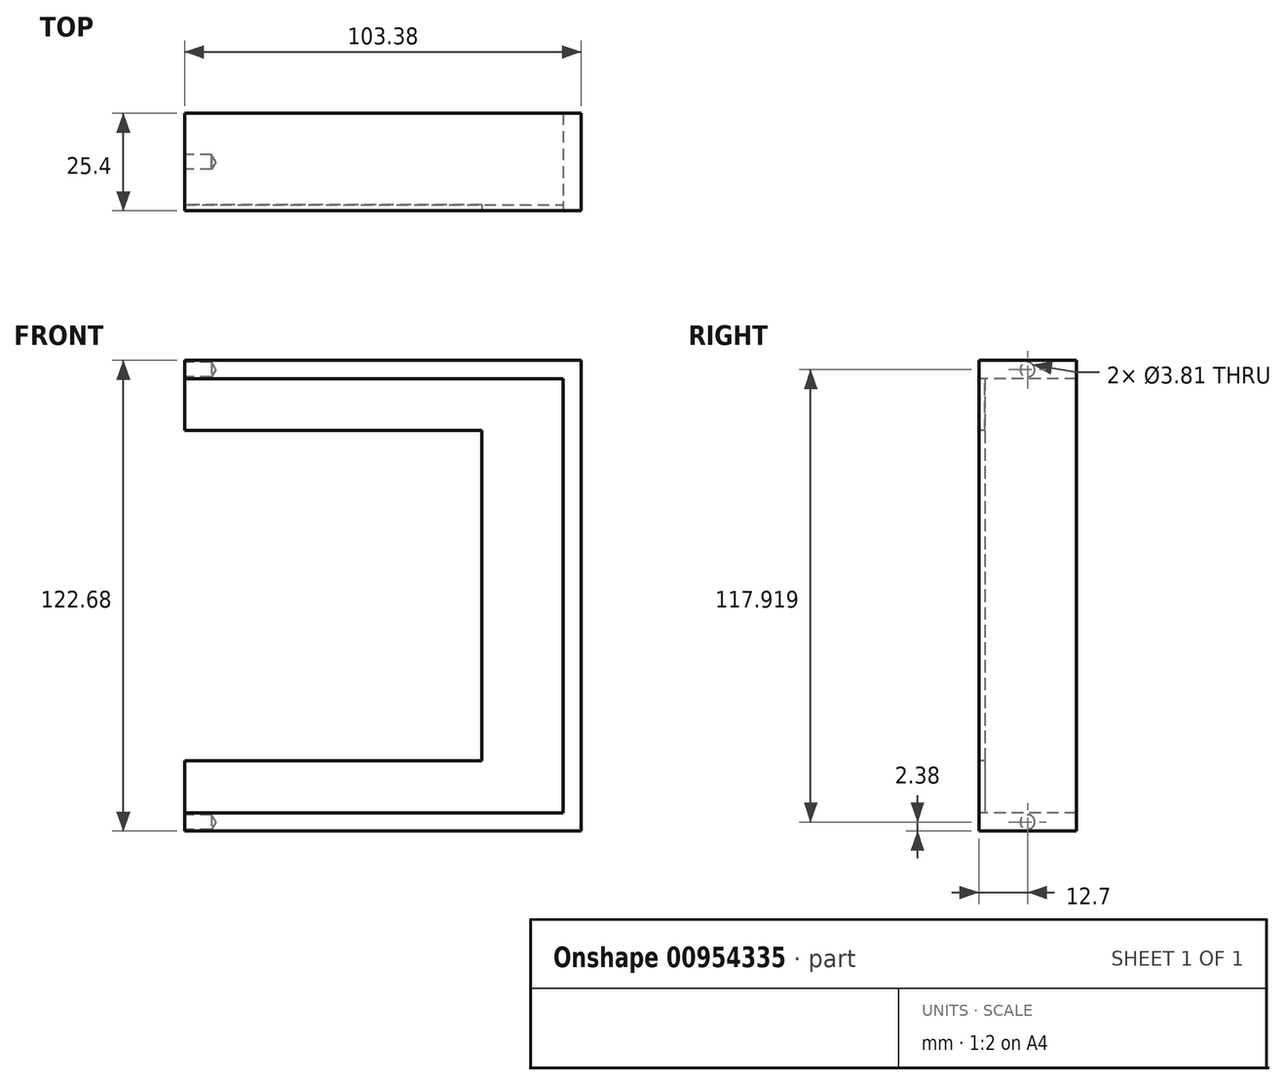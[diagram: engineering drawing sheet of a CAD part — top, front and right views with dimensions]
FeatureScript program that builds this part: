
annotation { "Feature Type Name" : "Feature", "Feature Type Description" : "" }
export const myFeature = defineFeature(function(context is Context, id is Id, definition is map)
    precondition{}
    {
        {
            var Q0;
            Q0=qCreatedBy(makeId("Front.planeOp"),FACE);
            var sketch = newSketch(context, id + "F0", { "sketchPlane" : qUnion([Q0])});
            skLineSegment(sketch, "E0.bottom", {"start": v(77.47, 43.05) * mm, "end": v(-77.47, 43.05) * mm});
            skLineSegment(sketch, "E0.top", {"start": v(77.47, -43.05) * mm, "end": v(-77.47, -43.05) * mm});
            skLineSegment(sketch, "E0.left", {"start": v(77.47, 43.05) * mm, "end": v(77.47, -43.05) * mm});
            skLineSegment(sketch, "E0.right", {"start": v(-77.47, 43.05) * mm, "end": v(-77.47, -43.05) * mm});
            skPoint(sketch, "E0.middle", {"position": v(0, 0) * mm});
            skLineSegment(sketch, "E1.bottom", {"start": v(-97.03, 55) * mm, "end": v(97.03, 55) * mm});
            skLineSegment(sketch, "E1.top", {"start": v(-97.03, -55) * mm, "end": v(97.03, -55) * mm});
            skLineSegment(sketch, "E1.left", {"start": v(-97.03, 55) * mm, "end": v(-97.03, -55) * mm});
            skLineSegment(sketch, "E1.right", {"start": v(97.03, 55) * mm, "end": v(97.03, -55) * mm});
            skLineSegment(sketch, "E2.0", {"start": v(-98.62, 56.58) * mm, "end": v(-98.62, -56.58) * mm});
            skLineSegment(sketch, "E2.1", {"start": v(-98.62, 56.58) * mm, "end": v(98.62, 56.58) * mm});
            skLineSegment(sketch, "E2.2", {"start": v(98.62, 56.58) * mm, "end": v(98.62, -56.58) * mm});
            skLineSegment(sketch, "E2.3", {"start": v(-98.62, -56.58) * mm, "end": v(98.62, -56.58) * mm});
            skLineSegment(sketch, "E3.0", {"start": v(-103.38, 61.34) * mm, "end": v(-103.38, -61.34) * mm});
            skLineSegment(sketch, "E3.1", {"start": v(-103.38, 61.34) * mm, "end": v(103.38, 61.34) * mm});
            skLineSegment(sketch, "E3.2", {"start": v(103.38, 61.34) * mm, "end": v(103.38, -61.34) * mm});
            skLineSegment(sketch, "E3.3", {"start": v(-103.38, -61.34) * mm, "end": v(103.38, -61.34) * mm});
            skLineSegment(sketch, "E4", {"start": v(0, 43.05) * mm, "end": v(0, 61.34) * mm});
            skLineSegment(sketch, "E5", {"start": v(0, -43.05) * mm, "end": v(0, -61.34) * mm});
            skSolve(sketch);
        }
        {
            var Q0;
            {var subQ0=sQuery(id+"F0.wireOp",EDGE,"E1.right");Q0=makeQuery(id+"F0.imprint","IMPRINT",FACE,{"disambiguationData":[TD([[makeQuery(id+"F0.imprint","IMPRINT",EDGE,{"derivedFrom":subQ0}),1.0]])]});}
            var Q1;
            {var subQ0=sQuery(id+"F0.wireOp",EDGE,"E0.left");Q1=makeQuery(id+"F0.imprint","IMPRINT",FACE,{"disambiguationData":[TD([[makeQuery(id+"F0.imprint","IMPRINT",EDGE,{"derivedFrom":subQ0}),1.0]])]});}
            extrude(context, id + "F1", {"entities" : qUnion([Q0, Q1]), "oppositeDirection" : true, "depth" : 1.59 * mm, "offsetDistance" : 25.4 * mm});
        }
        {
            var Q0;
            {var subQ1=sQuery(id+"F0.wireOp",EDGE,"E2.2");Q0=makeQuery(id+"F0.imprint","IMPRINT",FACE,{"disambiguationData":[TD([[makeQuery(id+"F0.imprint","IMPRINT",EDGE,{"derivedFrom":subQ1}),1.0]])]});}
            extrude(context, id + "F2", {"entities" : qUnion([Q0]), "oppositeDirection" : true, "depth" : 25.4 * mm, "offsetDistance" : 25.4 * mm});
        }
        {
            var Q0;
            Q0=makeQuery(id+"F2.opExtrude","SWEPT_FACE",FACE,{"disambiguationData":[OSD([sQuery(id+"F0.wireOp",EDGE,"E4")])]});
            var sketch = newSketch(context, id + "F3", { "sketchPlane" : qUnion([Q0])});
            skCircle(sketch, "E6", {"center": v(-12.7, 58.96) * mm, "radius": 1.9 * mm});
            skSolve(sketch);
        }
        {
            var Q0;
            Q0=sQuery(id+"F3.wireOp",VERTEX,"E6.center");
            var Q1;
            Q1=makeQuery(id+"F2.opExtrude","SWEPT_BODY",BODY,{"disambiguationData":[OSD([sQuery(id+"F0.wireOp",EDGE,"E2.1"),sQuery(id+"F0.wireOp",EDGE,"E2.2"),sQuery(id+"F0.wireOp",EDGE,"E2.3"),sQuery(id+"F0.wireOp",EDGE,"E3.1"),sQuery(id+"F0.wireOp",EDGE,"E3.2"),sQuery(id+"F0.wireOp",EDGE,"E3.3"),sQuery(id+"F0.wireOp",EDGE,"E4"),sQuery(id+"F0.wireOp",EDGE,"E5")])]});
            hole(context, id + "F4", {"style" : HoleStyle.SIMPLE, "endStyle" : HoleEndStyle.BLIND, "holeDiameter" : 3.8 * mm, "majorDiameter" : 6.35 * mm, "holeDepth" : 7 * mm, "isTappedThrough" : true, "tappedDepth" : 12.7 * mm, "tapClearance" : 3, "locations" : qUnion([Q0]), "scope" : qUnion([Q1])});
        }
        {
            var Q0;
            Q0=makeQuery(id+"F2.opExtrude","SWEPT_FACE",FACE,{"disambiguationData":[OSD([sQuery(id+"F0.wireOp",EDGE,"E5")])]});
            var sketch = newSketch(context, id + "F5", { "sketchPlane" : qUnion([Q0])});
            skCircle(sketch, "E7", {"center": v(-12.7, -58.96) * mm, "radius": 1.9 * mm});
            skSolve(sketch);
        }
        {
            var Q0;
            Q0=sQuery(id+"F5.wireOp",VERTEX,"E7.center");
            var Q1;
            Q1=makeQuery(id+"F2.opExtrude","SWEPT_BODY",BODY,{"disambiguationData":[OSD([sQuery(id+"F0.wireOp",EDGE,"E2.1"),sQuery(id+"F0.wireOp",EDGE,"E2.2"),sQuery(id+"F0.wireOp",EDGE,"E2.3"),sQuery(id+"F0.wireOp",EDGE,"E3.1"),sQuery(id+"F0.wireOp",EDGE,"E3.2"),sQuery(id+"F0.wireOp",EDGE,"E3.3"),sQuery(id+"F0.wireOp",EDGE,"E4"),sQuery(id+"F0.wireOp",EDGE,"E5")])]});
            hole(context, id + "F6", {"style" : HoleStyle.SIMPLE, "endStyle" : HoleEndStyle.BLIND, "holeDiameter" : 3.8 * mm, "majorDiameter" : 6.35 * mm, "holeDepth" : 7 * mm, "isTappedThrough" : true, "tappedDepth" : 12.7 * mm, "tapClearance" : 3, "locations" : qUnion([Q0]), "scope" : qUnion([Q1])});
        }
    });
